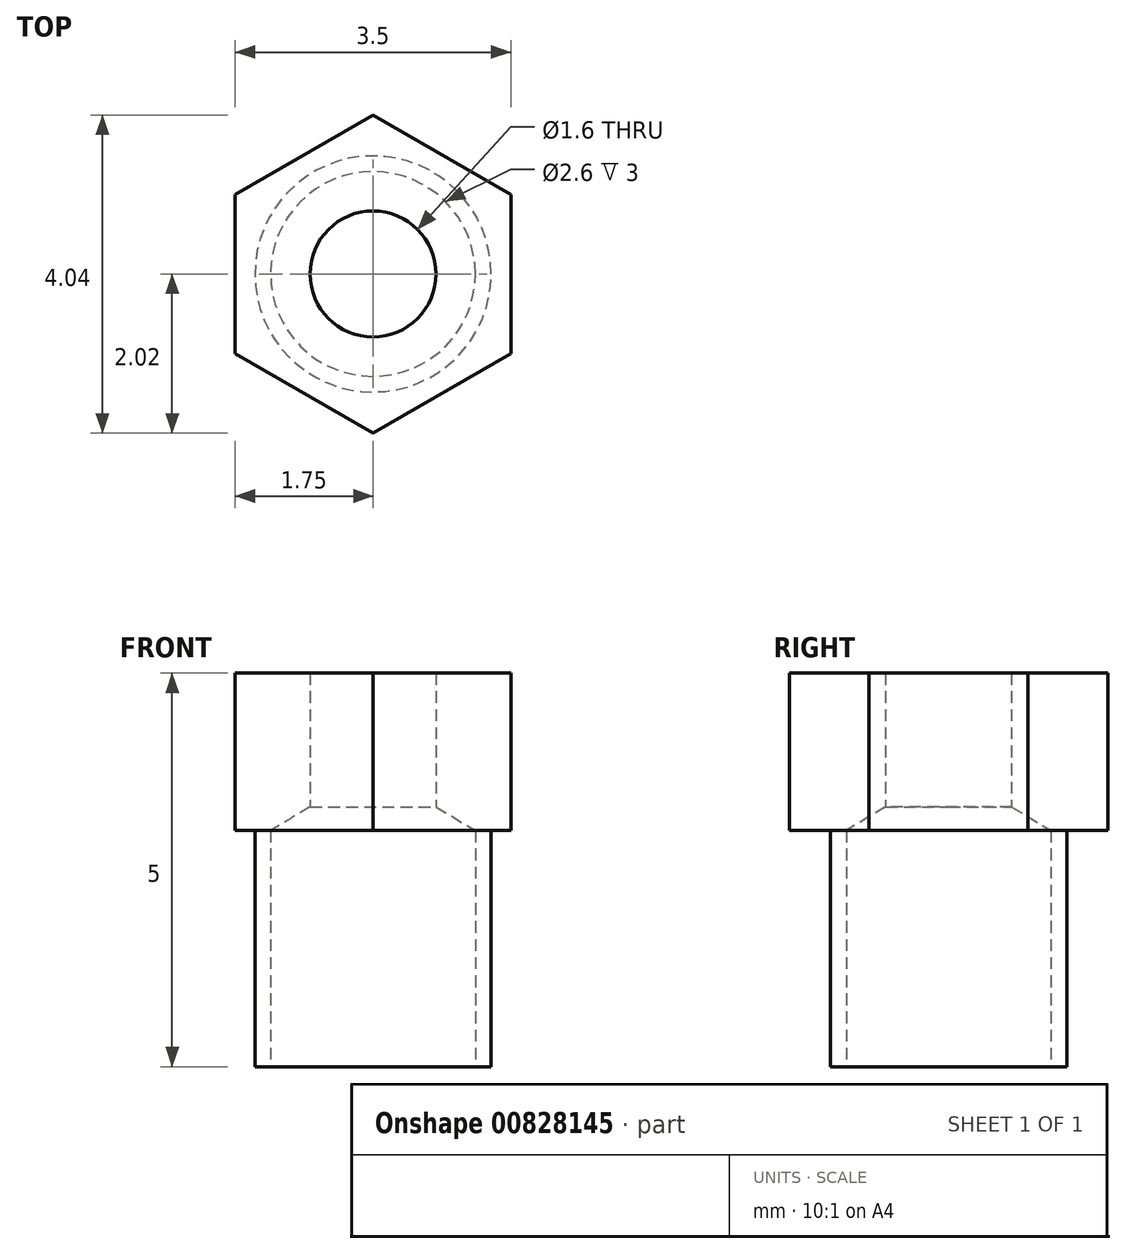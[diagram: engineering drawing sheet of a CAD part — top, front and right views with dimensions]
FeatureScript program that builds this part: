
annotation { "Feature Type Name" : "Feature", "Feature Type Description" : "" }
export const myFeature = defineFeature(function(context is Context, id is Id, definition is map)
    precondition{}
    {
        {
            var Q0;
            Q0=qCreatedBy(makeId("Top.planeOp"),FACE);
            var sketch = newSketch(context, id + "F0", { "sketchPlane" : qUnion([Q0])});
            skCircle(sketch, "E0.cCircle", {"center": v(0, 0) * mm, "radius": 1.75 * mm, "construction": true});
            skLineSegment(sketch, "E0.0", {"start": v(1.75, 1.01) * mm, "end": v(1.75, -1.01) * mm});
            skLineSegment(sketch, "E0.1", {"start": v(1.75, -1.01) * mm, "end": v(0, -2.02) * mm});
            skLineSegment(sketch, "E0.2", {"start": v(0, -2.02) * mm, "end": v(-1.75, -1.01) * mm});
            skLineSegment(sketch, "E0.3", {"start": v(-1.75, -1.01) * mm, "end": v(-1.75, 1.01) * mm});
            skLineSegment(sketch, "E0.4", {"start": v(-1.75, 1.01) * mm, "end": v(0, 2.02) * mm});
            skLineSegment(sketch, "E0.5", {"start": v(0, 2.02) * mm, "end": v(1.75, 1.01) * mm});
            skPoint(sketch, "E0.0.midPoint", {"position": v(1.75, 0) * mm});
            skCircle(sketch, "E1", {"center": v(0, 0) * mm, "radius": 0.8 * mm});
            skSolve(sketch);
        }
        {
            var Q0;
            Q0 = qSketchRegion(id + "F0", true);
            extrude(context, id + "F1", {"entities" : qUnion([Q0]), "depth" : 2 * mm, "offsetDistance" : 25 * mm});
        }
        {
            var Q0;
            Q0=makeQuery(id+"F1.opExtrude","CAP_FACE",FACE,{"disambiguationData":[OSD([sQuery(id+"F0.wireOp",EDGE,"E0.0"),sQuery(id+"F0.wireOp",EDGE,"E0.1"),sQuery(id+"F0.wireOp",EDGE,"E0.2"),sQuery(id+"F0.wireOp",EDGE,"E0.3"),sQuery(id+"F0.wireOp",EDGE,"E0.4"),sQuery(id+"F0.wireOp",EDGE,"E0.5"),sQuery(id+"F0.wireOp",EDGE,"E1")])],"isStart":true});
            var sketch = newSketch(context, id + "F2", { "sketchPlane" : qUnion([Q0])});
            skCircle(sketch, "E2", {"center": v(0, 0) * mm, "radius": 1.5 * mm});
            skSolve(sketch);
        }
        {
            var Q0;
            Q0 = qSketchRegion(id + "F2", true);
            extrude(context, id + "F3", {"entities" : qUnion([Q0]), "operationType" : NewBodyOperationType.ADD, "depth" : 3 * mm, "offsetDistance" : 25 * mm});
        }
        {
            var Q0;
            Q0=makeQuery(id+"F3.opExtrude","CAP_FACE",FACE,{"disambiguationData":[OSD([sQuery(id+"F2.wireOp",EDGE,"E2")])],"isStart":false});
            var sketch = newSketch(context, id + "F4", { "sketchPlane" : qUnion([Q0])});
            skPoint(sketch, "E3", {"position": v(0, 0) * mm});
            skSolve(sketch);
        }
        {
            var Q0;
            Q0=sQuery(id+"F4.wireOp",VERTEX,"E3");
            var Q1;
            Q1=makeQuery(id+"F1.opExtrude","SWEPT_BODY",BODY,{"disambiguationData":[OSD([sQuery(id+"F0.wireOp",EDGE,"E0.0"),sQuery(id+"F0.wireOp",EDGE,"E0.1"),sQuery(id+"F0.wireOp",EDGE,"E0.2"),sQuery(id+"F0.wireOp",EDGE,"E0.3"),sQuery(id+"F0.wireOp",EDGE,"E0.4"),sQuery(id+"F0.wireOp",EDGE,"E0.5"),sQuery(id+"F0.wireOp",EDGE,"E1")])]});
            hole(context, id + "F5", {"style" : HoleStyle.SIMPLE, "endStyle" : HoleEndStyle.BLIND, "holeDiameter" : 2.6 * mm, "majorDiameter" : 5 * mm, "holeDepth" : 3 * mm, "isTappedThrough" : true, "tappedDepth" : 7.3 * mm, "tapClearance" : 3, "locations" : qUnion([Q0]), "scope" : qUnion([Q1])});
        }
    });
